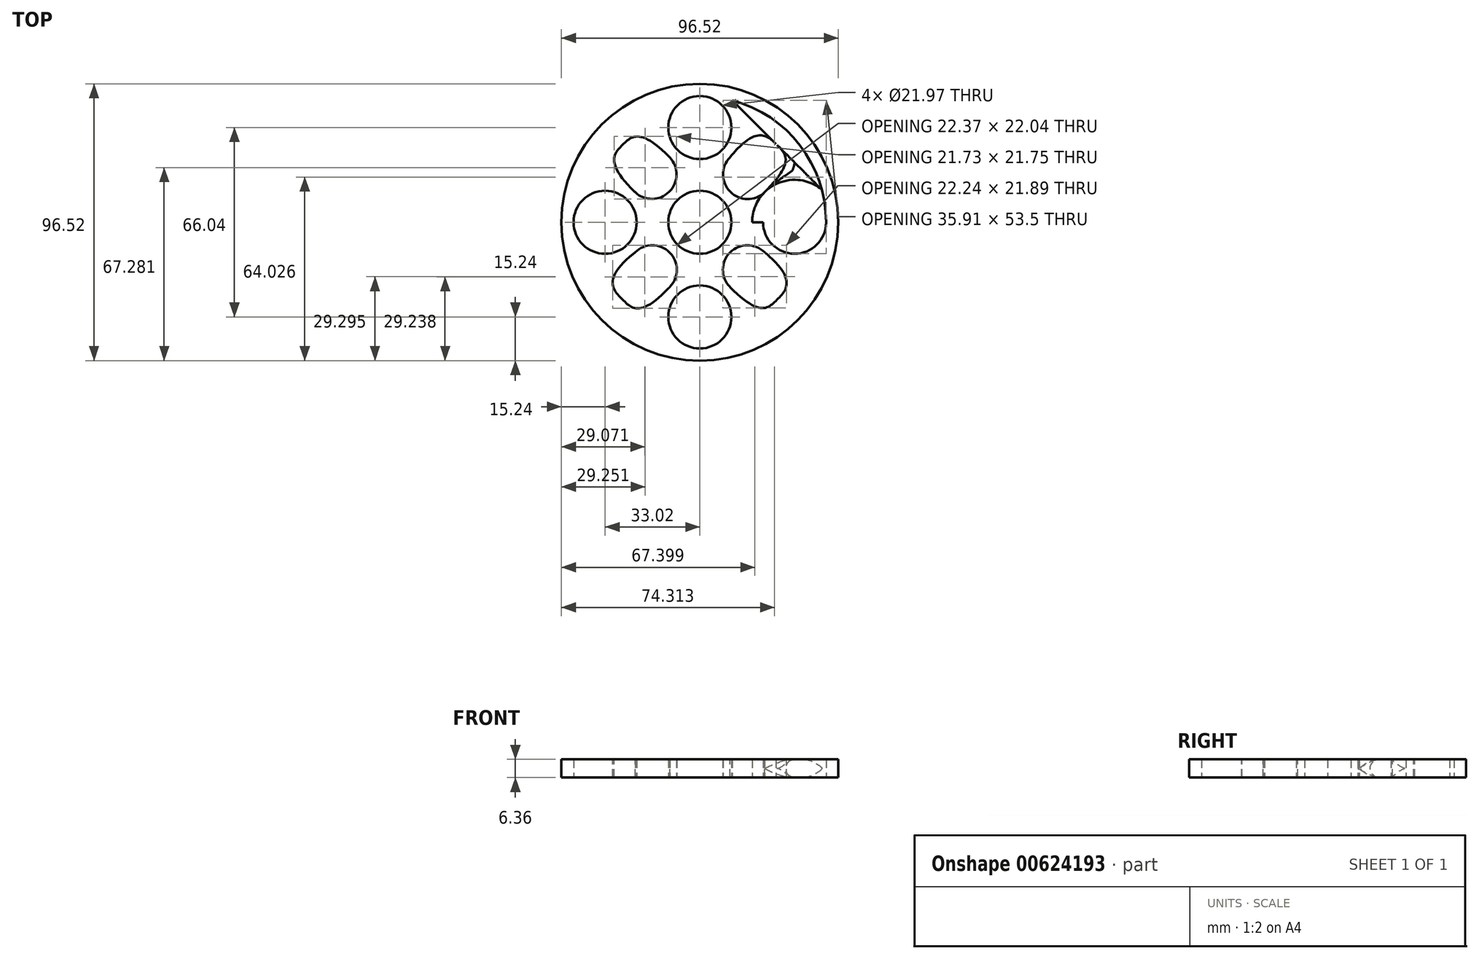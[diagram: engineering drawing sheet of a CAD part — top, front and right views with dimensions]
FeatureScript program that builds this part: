
annotation { "Feature Type Name" : "Feature", "Feature Type Description" : "" }
export const myFeature = defineFeature(function(context is Context, id is Id, definition is map)
    precondition{}
    {
        {
            var Q0;
            Q0=qCreatedBy(makeId("Top.planeOp"),FACE);
            var sketch = newSketch(context, id + "F0", { "sketchPlane" : qUnion([Q0])});
            skCircle(sketch, "E0", {"center": v(0, 0) * mm, "radius": 10.99 * mm});
            skCircle(sketch, "E1", {"center": v(0, 0) * mm, "radius": 14.8 * mm});
            skLineSegment(sketch, "E2", {"start": v(0, 0) * mm, "end": v(0, 33.02) * mm});
            skCircle(sketch, "E3", {"center": v(0, 33.02) * mm, "radius": 10.99 * mm});
            skCircle(sketch, "E4", {"center": v(0, 33.02) * mm, "radius": 14.8 * mm});
            skLineSegment(sketch, "E5.1.0", {"start": v(0, 0) * mm, "end": v(-33.02, 0) * mm});
            skCircle(sketch, "E5.1.1", {"center": v(-33.02, 0) * mm, "radius": 10.99 * mm});
            skCircle(sketch, "E5.1.2", {"center": v(-33.02, 0) * mm, "radius": 14.8 * mm});
            skLineSegment(sketch, "E5.2.0", {"start": v(0, 0) * mm, "end": v(0, -33.02) * mm});
            skCircle(sketch, "E5.2.1", {"center": v(0, -33.02) * mm, "radius": 10.99 * mm});
            skCircle(sketch, "E5.2.2", {"center": v(0, -33.02) * mm, "radius": 14.8 * mm});
            skLineSegment(sketch, "E6.2.3.0", {"start": v(0, 0) * mm, "end": v(33.02, 0) * mm});
            skCircle(sketch, "E6.3.3.0", {"center": v(33.02, 0) * mm, "radius": 10.99 * mm});
            skCircle(sketch, "E6.5.3.0", {"center": v(33.02, 0) * mm, "radius": 14.8 * mm});
            skPoint(sketch, "E7", {"position": v(-22.56, 10.46) * mm});
            skPoint(sketch, "E8", {"position": v(-10.46, 22.56) * mm});
            skPoint(sketch, "E9", {"position": v(10.46, 22.56) * mm});
            skPoint(sketch, "E10", {"position": v(22.56, 10.46) * mm});
            skPoint(sketch, "E11", {"position": v(22.56, -10.46) * mm});
            skPoint(sketch, "E12", {"position": v(10.46, -22.56) * mm});
            skPoint(sketch, "E13", {"position": v(-10.46, -22.56) * mm});
            skPoint(sketch, "E14", {"position": v(-22.56, -10.46) * mm});
            skArc(sketch, "E15", {"start": v(-22.56, 10.46) * mm, "mid": v(-10.65, 10.65) * mm, "end": v(-10.46, 22.56) * mm});
            skArc(sketch, "E16", {"start": v(10.46, 22.56) * mm, "mid": v(10.6, 10.6) * mm, "end": v(22.56, 10.46) * mm});
            skArc(sketch, "E17", {"start": v(22.56, -10.46) * mm, "mid": v(10.53, -10.53) * mm, "end": v(10.46, -22.56) * mm});
            skArc(sketch, "E18", {"start": v(-10.46, -22.56) * mm, "mid": v(-10.5, -10.5) * mm, "end": v(-22.56, -10.46) * mm});
            skCircle(sketch, "E19", {"center": v(0, 0) * mm, "radius": 44 * mm});
            skCircle(sketch, "E20", {"center": v(0, 0) * mm, "radius": 48.26 * mm});
            skLineSegment(sketch, "E21", {"start": v(42.52, 11.34) * mm, "end": v(11.34, 42.52) * mm});
            skLineSegment(sketch, "E22", {"start": v(-11.34, 42.52) * mm, "end": v(-42.49, 11.45) * mm});
            skLineSegment(sketch, "E23", {"start": v(-42.52, -11.34) * mm, "end": v(-11.45, -42.49) * mm});
            skLineSegment(sketch, "E24", {"start": v(11.34, -42.52) * mm, "end": v(42.49, -11.45) * mm});
            skFitSpline(sketch, "E25", {"points": [v(22.56, 10.46) * mm, v(26.93, 26.93) * mm, v(10.46, 22.56) * mm], "startDerivative": vector(62.37, 62.42) * mm, "endDerivative": vector(-55.65, -69.41) * mm});
            skFitSpline(sketch, "E26", {"points": [v(-10.46, 22.56) * mm, v(-26.92, 26.98) * mm, v(-22.56, 10.46) * mm], "startDerivative": vector(-61.8, 63.48) * mm, "endDerivative": vector(63.5, -61.8) * mm});
            skFitSpline(sketch, "E27", {"points": [v(-22.56, -10.46) * mm, v(-26.98, -26.92) * mm, v(-10.46, -22.56) * mm], "startDerivative": vector(-69.52, -55.75) * mm, "endDerivative": vector(60.94, 64.35) * mm});
            skFitSpline(sketch, "E28", {"points": [v(10.46, -22.56) * mm, v(26.92, -26.99) * mm, v(22.56, -10.46) * mm], "startDerivative": vector(62.67, -62.62) * mm, "endDerivative": vector(-68.67, 56.64) * mm});
            skSolve(sketch);
        }
        {
            var Q0;
            Q0=makeQuery(id+"F0.imprint","IMPRINT",FACE,{"disambiguationData":[TD([[makeQuery(id+"F0.imprint","IMPRINT",EDGE,{"derivedFrom":sQuery(id+"F0.wireOp",EDGE,"E5.1.1")}),-1.0]])]});
            var Q1;
            Q1=makeQuery(id+"F0.imprint","IMPRINT",FACE,{"disambiguationData":[TD([[makeQuery(id+"F0.imprint","IMPRINT",EDGE,{"derivedFrom":sQuery(id+"F0.wireOp",EDGE,"E5.2.1")}),-1.0]])]});
            var Q2;
            Q2=makeQuery(id+"F0.imprint","IMPRINT",FACE,{"disambiguationData":[TD([[makeQuery(id+"F0.imprint","IMPRINT",EDGE,{"derivedFrom":sQuery(id+"F0.wireOp",EDGE,"E6.3.3.0")}),-1.0]])]});
            var Q3;
            Q3=makeQuery(id+"F0.imprint","IMPRINT",FACE,{"disambiguationData":[TD([[makeQuery(id+"F0.imprint","IMPRINT",EDGE,{"derivedFrom":sQuery(id+"F0.wireOp",EDGE,"E3")}),-1.0]])]});
            var Q4;
            {var subQ0=sQuery(id+"F0.wireOp",EDGE,"E2");var subQ1=sQuery(id+"F0.wireOp",EDGE,"E0");var subQ2=makeQuery(id+"F0.imprint","INTERSECT",VERTEX,{"derivedFrom":[subQ1,subQ0]});Q4=makeQuery(id+"F0.imprint","IMPRINT",FACE,{"disambiguationData":[TD([[makeQuery(id+"F0.imprint","IMPRINT",EDGE,{"disambiguationData":[TD([[subQ2,1.0]])],"derivedFrom":subQ1}),-1.0]])]});}
            var Q5;
            {var subQ0=sQuery(id+"F0.wireOp",EDGE,"E6.2.3.0");var subQ1=sQuery(id+"F0.wireOp",EDGE,"E0");var subQ2=makeQuery(id+"F0.imprint","INTERSECT",VERTEX,{"derivedFrom":[subQ1,subQ0]});Q5=makeQuery(id+"F0.imprint","IMPRINT",FACE,{"disambiguationData":[TD([[makeQuery(id+"F0.imprint","IMPRINT",EDGE,{"disambiguationData":[TD([[subQ2,1.0]])],"derivedFrom":subQ1}),-1.0]])]});}
            var Q6;
            {var subQ0=sQuery(id+"F0.wireOp",EDGE,"E5.1.0");var subQ1=sQuery(id+"F0.wireOp",EDGE,"E0");var subQ2=makeQuery(id+"F0.imprint","INTERSECT",VERTEX,{"derivedFrom":[subQ1,subQ0]});Q6=makeQuery(id+"F0.imprint","IMPRINT",FACE,{"disambiguationData":[TD([[makeQuery(id+"F0.imprint","IMPRINT",EDGE,{"disambiguationData":[TD([[subQ2,-1.0]])],"derivedFrom":subQ1}),-1.0]])]});}
            var Q7;
            {var subQ0=sQuery(id+"F0.wireOp",EDGE,"E2");var subQ1=sQuery(id+"F0.wireOp",EDGE,"E0");var subQ2=makeQuery(id+"F0.imprint","INTERSECT",VERTEX,{"derivedFrom":[subQ1,subQ0]});Q7=makeQuery(id+"F0.imprint","IMPRINT",FACE,{"disambiguationData":[TD([[makeQuery(id+"F0.imprint","IMPRINT",EDGE,{"disambiguationData":[TD([[subQ2,-1.0]])],"derivedFrom":subQ1}),-1.0]])]});}
            var Q8;
            {var subQ5=sQuery(id+"F0.wireOp",EDGE,"E18");Q8=makeQuery(id+"F0.imprint","IMPRINT",FACE,{"disambiguationData":[TD([[makeQuery(id+"F0.imprint","IMPRINT",EDGE,{"derivedFrom":subQ5}),-1.0]])]});}
            var Q9;
            {var subQ5=sQuery(id+"F0.wireOp",EDGE,"E16");Q9=makeQuery(id+"F0.imprint","IMPRINT",FACE,{"disambiguationData":[TD([[makeQuery(id+"F0.imprint","IMPRINT",EDGE,{"derivedFrom":subQ5}),-1.0]])]});}
            var Q10;
            {var subQ5=sQuery(id+"F0.wireOp",EDGE,"E17");Q10=makeQuery(id+"F0.imprint","IMPRINT",FACE,{"disambiguationData":[TD([[makeQuery(id+"F0.imprint","IMPRINT",EDGE,{"derivedFrom":subQ5}),-1.0]])]});}
            var Q11;
            {var subQ5=sQuery(id+"F0.wireOp",EDGE,"E15");Q11=makeQuery(id+"F0.imprint","IMPRINT",FACE,{"disambiguationData":[TD([[makeQuery(id+"F0.imprint","IMPRINT",EDGE,{"derivedFrom":subQ5}),-1.0]])]});}
            var Q12;
            Q12=makeQuery(id+"F0.imprint","IMPRINT",FACE,{"disambiguationData":[TD([[makeQuery(id+"F0.imprint","IMPRINT",EDGE,{"derivedFrom":sQuery(id+"F0.wireOp",EDGE,"E20")}),1.0]])]});
            var Q13;
            {var subQ0=sQuery(id+"F0.wireOp",EDGE,"E19");var subQ1=sQuery(id+"F0.wireOp",EDGE,"E4");var subQ2=makeQuery(id+"F0.imprint","INTERSECT",VERTEX,{"disambiguationData":[OD(0.0)],"derivedFrom":[subQ1,subQ0]});Q13=makeQuery(id+"F0.imprint","IMPRINT",FACE,{"disambiguationData":[TD([[makeQuery(id+"F0.imprint","IMPRINT",EDGE,{"disambiguationData":[TD([[subQ2,1.0]])],"derivedFrom":subQ1}),1.0]])]});}
            var Q14;
            {var subQ0=sQuery(id+"F0.wireOp",EDGE,"E19");var subQ1=sQuery(id+"F0.wireOp",EDGE,"E5.1.2");var subQ2=makeQuery(id+"F0.imprint","INTERSECT",VERTEX,{"disambiguationData":[OD(0.0)],"derivedFrom":[subQ1,subQ0]});Q14=makeQuery(id+"F0.imprint","IMPRINT",FACE,{"disambiguationData":[TD([[makeQuery(id+"F0.imprint","IMPRINT",EDGE,{"disambiguationData":[TD([[subQ2,1.0]])],"derivedFrom":subQ1}),1.0]])]});}
            var Q15;
            {var subQ0=sQuery(id+"F0.wireOp",EDGE,"E19");var subQ1=sQuery(id+"F0.wireOp",EDGE,"E5.2.2");var subQ2=makeQuery(id+"F0.imprint","INTERSECT",VERTEX,{"disambiguationData":[OD(0.0)],"derivedFrom":[subQ1,subQ0]});Q15=makeQuery(id+"F0.imprint","IMPRINT",FACE,{"disambiguationData":[TD([[makeQuery(id+"F0.imprint","IMPRINT",EDGE,{"disambiguationData":[TD([[subQ2,1.0]])],"derivedFrom":subQ1}),1.0]])]});}
            var Q16;
            {var subQ0=sQuery(id+"F0.wireOp",EDGE,"E19");var subQ1=sQuery(id+"F0.wireOp",EDGE,"E6.5.3.0");var subQ2=makeQuery(id+"F0.imprint","INTERSECT",VERTEX,{"disambiguationData":[OD(0.0)],"derivedFrom":[subQ1,subQ0]});Q16=makeQuery(id+"F0.imprint","IMPRINT",FACE,{"disambiguationData":[TD([[makeQuery(id+"F0.imprint","IMPRINT",EDGE,{"disambiguationData":[TD([[subQ2,1.0]])],"derivedFrom":subQ1}),1.0]])]});}
            var Q17;
            {var subQ0=sQuery(id+"F0.wireOp",EDGE,"E25");var subQ3=sQuery(id+"F0.wireOp",EDGE,"E21");var subQ5=makeQuery(id+"F0.imprint","INTERSECT",VERTEX,{"derivedFrom":[subQ3,subQ0]});Q17=makeQuery(id+"F0.imprint","IMPRINT",FACE,{"disambiguationData":[TD([[makeQuery(id+"F0.imprint","IMPRINT",EDGE,{"disambiguationData":[TD([[subQ5,1.0]])],"derivedFrom":subQ3}),1.0]])]});}
            var Q18;
            {var subQ0=sQuery(id+"F0.wireOp",EDGE,"E25");var subQ3=sQuery(id+"F0.wireOp",EDGE,"E21");var subQ5=makeQuery(id+"F0.imprint","INTERSECT",VERTEX,{"derivedFrom":[subQ3,subQ0]});Q18=makeQuery(id+"F0.imprint","IMPRINT",FACE,{"disambiguationData":[TD([[makeQuery(id+"F0.imprint","IMPRINT",EDGE,{"disambiguationData":[TD([[subQ5,-1.0]])],"derivedFrom":subQ3}),1.0]])]});}
            var Q19;
            {var subQ0=sQuery(id+"F0.wireOp",EDGE,"E26");var subQ3=sQuery(id+"F0.wireOp",EDGE,"E22");var subQ5=makeQuery(id+"F0.imprint","INTERSECT",VERTEX,{"derivedFrom":[subQ3,subQ0]});Q19=makeQuery(id+"F0.imprint","IMPRINT",FACE,{"disambiguationData":[TD([[makeQuery(id+"F0.imprint","IMPRINT",EDGE,{"disambiguationData":[TD([[subQ5,1.0]])],"derivedFrom":subQ3}),1.0]])]});}
            var Q20;
            {var subQ3=sQuery(id+"F0.wireOp",EDGE,"E19");var subQ5=sQuery(id+"F0.wireOp",EDGE,"E22");var subQ6=makeQuery(id+"F0.imprint","INTERSECT",VERTEX,{"derivedFrom":[subQ3,subQ5]});Q20=makeQuery(id+"F0.imprint","IMPRINT",FACE,{"disambiguationData":[TD([[makeQuery(id+"F0.imprint","IMPRINT",EDGE,{"disambiguationData":[TD([[subQ6,-1.0]])],"derivedFrom":subQ3}),1.0]])]});}
            var Q21;
            {var subQ0=sQuery(id+"F0.wireOp",EDGE,"E27");var subQ3=sQuery(id+"F0.wireOp",EDGE,"E23");var subQ5=makeQuery(id+"F0.imprint","INTERSECT",VERTEX,{"derivedFrom":[subQ3,subQ0]});Q21=makeQuery(id+"F0.imprint","IMPRINT",FACE,{"disambiguationData":[TD([[makeQuery(id+"F0.imprint","IMPRINT",EDGE,{"disambiguationData":[TD([[subQ5,1.0]])],"derivedFrom":subQ3}),1.0]])]});}
            var Q22;
            {var subQ3=sQuery(id+"F0.wireOp",EDGE,"E19");var subQ5=sQuery(id+"F0.wireOp",EDGE,"E23");var subQ6=makeQuery(id+"F0.imprint","INTERSECT",VERTEX,{"derivedFrom":[subQ3,subQ5]});Q22=makeQuery(id+"F0.imprint","IMPRINT",FACE,{"disambiguationData":[TD([[makeQuery(id+"F0.imprint","IMPRINT",EDGE,{"disambiguationData":[TD([[subQ6,-1.0]])],"derivedFrom":subQ3}),1.0]])]});}
            var Q23;
            {var subQ0=sQuery(id+"F0.wireOp",EDGE,"E28");var subQ3=sQuery(id+"F0.wireOp",EDGE,"E24");var subQ5=makeQuery(id+"F0.imprint","INTERSECT",VERTEX,{"derivedFrom":[subQ3,subQ0]});Q23=makeQuery(id+"F0.imprint","IMPRINT",FACE,{"disambiguationData":[TD([[makeQuery(id+"F0.imprint","IMPRINT",EDGE,{"disambiguationData":[TD([[subQ5,1.0]])],"derivedFrom":subQ3}),1.0]])]});}
            var Q24;
            {var subQ3=sQuery(id+"F0.wireOp",EDGE,"E19");var subQ5=sQuery(id+"F0.wireOp",EDGE,"E24");var subQ6=makeQuery(id+"F0.imprint","INTERSECT",VERTEX,{"derivedFrom":[subQ3,subQ5]});Q24=makeQuery(id+"F0.imprint","IMPRINT",FACE,{"disambiguationData":[TD([[makeQuery(id+"F0.imprint","IMPRINT",EDGE,{"disambiguationData":[TD([[subQ6,-1.0]])],"derivedFrom":subQ3}),1.0]])]});}
            var Q25;
            {var subQ0=sQuery(id+"F0.wireOp",EDGE,"E19");var subQ4=makeQuery(id+"F0.imprint","INTERSECT",VERTEX,{"derivedFrom":[sQuery(id+"F0.wireOp",EDGE,"E6.3.3.0"),subQ0]});Q25=makeQuery(id+"F0.imprint","IMPRINT",FACE,{"disambiguationData":[TD([[makeQuery(id+"F0.imprint","IMPRINT",EDGE,{"disambiguationData":[TD([[subQ4,1.0]])],"derivedFrom":subQ0}),-1.0]])]});}
            var Q26;
            {var subQ0=sQuery(id+"F0.wireOp",EDGE,"E19");var subQ4=makeQuery(id+"F0.imprint","INTERSECT",VERTEX,{"derivedFrom":[sQuery(id+"F0.wireOp",EDGE,"E5.2.1"),subQ0]});Q26=makeQuery(id+"F0.imprint","IMPRINT",FACE,{"disambiguationData":[TD([[makeQuery(id+"F0.imprint","IMPRINT",EDGE,{"disambiguationData":[TD([[subQ4,1.0]])],"derivedFrom":subQ0}),-1.0]])]});}
            var Q27;
            {var subQ0=sQuery(id+"F0.wireOp",EDGE,"E19");var subQ4=makeQuery(id+"F0.imprint","INTERSECT",VERTEX,{"derivedFrom":[sQuery(id+"F0.wireOp",EDGE,"E5.1.1"),subQ0]});Q27=makeQuery(id+"F0.imprint","IMPRINT",FACE,{"disambiguationData":[TD([[makeQuery(id+"F0.imprint","IMPRINT",EDGE,{"disambiguationData":[TD([[subQ4,1.0]])],"derivedFrom":subQ0}),-1.0]])]});}
            var Q28;
            {var subQ0=sQuery(id+"F0.wireOp",EDGE,"E19");var subQ1=sQuery(id+"F0.wireOp",EDGE,"E5.1.2");var subQ3=makeQuery(id+"F0.imprint","INTERSECT",VERTEX,{"derivedFrom":[subQ1,subQ0]});Q28=makeQuery(id+"F0.imprint","IMPRINT",FACE,{"disambiguationData":[TD([[makeQuery(id+"F0.imprint","IMPRINT",EDGE,{"disambiguationData":[TD([[subQ3,-1.0]])],"derivedFrom":subQ1}),1.0]])]});}
            var Q29;
            {var subQ1=sQuery(id+"F0.wireOp",EDGE,"E6.5.3.0");var subQ8=makeQuery(id+"F0.imprint","IMPRINT",VERTEX,{"derivedFrom":subQ1});Q29=makeQuery(id+"F0.imprint","IMPRINT",FACE,{"disambiguationData":[TD([[makeQuery(id+"F0.imprint","IMPRINT",EDGE,{"disambiguationData":[TD([[subQ8,1.0]])],"derivedFrom":subQ1}),1.0]])]});}
            var Q30;
            {var subQ0=sQuery(id+"F0.wireOp",EDGE,"E19");var subQ1=sQuery(id+"F0.wireOp",EDGE,"E5.2.2");var subQ3=makeQuery(id+"F0.imprint","INTERSECT",VERTEX,{"derivedFrom":[subQ1,subQ0]});Q30=makeQuery(id+"F0.imprint","IMPRINT",FACE,{"disambiguationData":[TD([[makeQuery(id+"F0.imprint","IMPRINT",EDGE,{"disambiguationData":[TD([[subQ3,-1.0]])],"derivedFrom":subQ1}),1.0]])]});}
            var Q31;
            {var subQ0=sQuery(id+"F0.wireOp",EDGE,"E23");var subQ1=sQuery(id+"F0.wireOp",EDGE,"E19");var subQ3=makeQuery(id+"F0.imprint","INTERSECT",VERTEX,{"derivedFrom":[subQ1,subQ0]});Q31=makeQuery(id+"F0.imprint","IMPRINT",FACE,{"disambiguationData":[TD([[makeQuery(id+"F0.imprint","IMPRINT",EDGE,{"disambiguationData":[TD([[subQ3,1.0]])],"derivedFrom":subQ0}),-1.0]])]});}
            var Q32;
            {var subQ0=sQuery(id+"F0.wireOp",EDGE,"E24");var subQ1=sQuery(id+"F0.wireOp",EDGE,"E19");var subQ3=makeQuery(id+"F0.imprint","INTERSECT",VERTEX,{"derivedFrom":[subQ1,subQ0]});Q32=makeQuery(id+"F0.imprint","IMPRINT",FACE,{"disambiguationData":[TD([[makeQuery(id+"F0.imprint","IMPRINT",EDGE,{"disambiguationData":[TD([[subQ3,1.0]])],"derivedFrom":subQ0}),-1.0]])]});}
            var Q33;
            {var subQ0=sQuery(id+"F0.wireOp",EDGE,"E21");var subQ4=sQuery(id+"F0.wireOp",EDGE,"E25");var subQ6=makeQuery(id+"F0.imprint","INTERSECT",VERTEX,{"disambiguationData":[OD(0.0)],"derivedFrom":[subQ0,subQ4]});Q33=makeQuery(id+"F0.imprint","IMPRINT",FACE,{"disambiguationData":[TD([[makeQuery(id+"F0.imprint","IMPRINT",EDGE,{"disambiguationData":[TD([[subQ6,-1.0]])],"derivedFrom":subQ4}),-1.0]])]});}
            var Q34;
            {var subQ0=sQuery(id+"F0.wireOp",EDGE,"E22");var subQ1=sQuery(id+"F0.wireOp",EDGE,"E19");var subQ3=makeQuery(id+"F0.imprint","INTERSECT",VERTEX,{"derivedFrom":[subQ1,subQ0]});Q34=makeQuery(id+"F0.imprint","IMPRINT",FACE,{"disambiguationData":[TD([[makeQuery(id+"F0.imprint","IMPRINT",EDGE,{"disambiguationData":[TD([[subQ3,1.0]])],"derivedFrom":subQ0}),-1.0]])]});}
            extrude(context, id + "F1", {"entities" : qUnion([Q0, Q1, Q2, Q3, Q4, Q5, Q6, Q7, Q8, Q9, Q10, Q11, Q12, Q13, Q14, Q15, Q16, Q17, Q18, Q19, Q20, Q21, Q22, Q23, Q24, Q25, Q26, Q27, Q28, Q29, Q30, Q31, Q32, Q33, Q34]), "endBound" : BoundingType.SYMMETRIC, "depth" : 6.35 * mm, "offsetDistance" : 25.4 * mm});
        }
        {
            var Q0;
            Q0=makeQuery(id+"F1.opExtrude","CAP_EDGE",EDGE,{"disambiguationData":[OSD([sQuery(id+"F0.wireOp",EDGE,"E15")])],"isStart":false});
            var Q1;
            Q1=makeQuery(id+"F1.opExtrude","CAP_EDGE",EDGE,{"disambiguationData":[OSD([sQuery(id+"F0.wireOp",EDGE,"E26")])],"isStart":false});
            var Q2;
            Q2=makeQuery(id+"F1.opExtrude","CAP_EDGE",EDGE,{"disambiguationData":[OSD([sQuery(id+"F0.wireOp",EDGE,"E16")])],"isStart":false});
            var Q3;
            Q3=makeQuery(id+"F1.opExtrude","CAP_EDGE",EDGE,{"disambiguationData":[OSD([sQuery(id+"F0.wireOp",EDGE,"E25")])],"isStart":false});
            var Q4;
            Q4=makeQuery(id+"F1.opExtrude","CAP_EDGE",EDGE,{"disambiguationData":[OSD([sQuery(id+"F0.wireOp",EDGE,"E6.5.3.0")])],"isStart":false});
            var Q5;
            Q5=makeQuery(id+"F1.opExtrude","CAP_EDGE",EDGE,{"disambiguationData":[OSD([sQuery(id+"F0.wireOp",EDGE,"E17")])],"isStart":false});
            var Q6;
            Q6=makeQuery(id+"F1.opExtrude","CAP_EDGE",EDGE,{"disambiguationData":[OSD([sQuery(id+"F0.wireOp",EDGE,"E28")])],"isStart":false});
            var Q7;
            Q7=makeQuery(id+"F1.opExtrude","CAP_EDGE",EDGE,{"disambiguationData":[OSD([sQuery(id+"F0.wireOp",EDGE,"E27")])],"isStart":false});
            var Q8;
            Q8=makeQuery(id+"F1.opExtrude","CAP_EDGE",EDGE,{"disambiguationData":[OSD([sQuery(id+"F0.wireOp",EDGE,"E18")])],"isStart":false});
            var Q9;
            Q9=makeQuery(id+"F1.opExtrude","CAP_EDGE",EDGE,{"disambiguationData":[OSD([sQuery(id+"F0.wireOp",EDGE,"E20")])],"isStart":false});
            var Q10;
            Q10=makeQuery(id+"F1.opExtrude","CAP_EDGE",EDGE,{"disambiguationData":[OSD([sQuery(id+"F0.wireOp",EDGE,"E20")])],"isStart":true});
            var Q11;
            Q11=makeQuery(id+"F1.opExtrude","CAP_EDGE",EDGE,{"disambiguationData":[OSD([sQuery(id+"F0.wireOp",EDGE,"E15")])],"isStart":true});
            var Q12;
            Q12=makeQuery(id+"F1.opExtrude","CAP_EDGE",EDGE,{"disambiguationData":[OSD([sQuery(id+"F0.wireOp",EDGE,"E26")])],"isStart":true});
            var Q13;
            Q13=makeQuery(id+"F1.opExtrude","CAP_EDGE",EDGE,{"disambiguationData":[OSD([sQuery(id+"F0.wireOp",EDGE,"E25")])],"isStart":true});
            var Q14;
            Q14=makeQuery(id+"F1.opExtrude","CAP_EDGE",EDGE,{"disambiguationData":[OSD([sQuery(id+"F0.wireOp",EDGE,"E6.5.3.0")])],"isStart":true});
            var Q15;
            Q15=makeQuery(id+"F1.opExtrude","CAP_EDGE",EDGE,{"disambiguationData":[OSD([sQuery(id+"F0.wireOp",EDGE,"E28")])],"isStart":true});
            var Q16;
            Q16=makeQuery(id+"F1.opExtrude","CAP_EDGE",EDGE,{"disambiguationData":[OSD([sQuery(id+"F0.wireOp",EDGE,"E17")])],"isStart":true});
            var Q17;
            Q17=makeQuery(id+"F1.opExtrude","CAP_EDGE",EDGE,{"disambiguationData":[OSD([sQuery(id+"F0.wireOp",EDGE,"E27")])],"isStart":true});
            var Q18;
            Q18=makeQuery(id+"F1.opExtrude","CAP_EDGE",EDGE,{"disambiguationData":[OSD([sQuery(id+"F0.wireOp",EDGE,"E18")])],"isStart":true});
            fillet(context, id + "F2", {"entities" : qUnion([Q0, Q1, Q2, Q3, Q4, Q5, Q6, Q7, Q8, Q9, Q10, Q11, Q12, Q13, Q14, Q15, Q16, Q17, Q18]), "radius" : 3.17 * mm, "tangentPropagation" : true, "allowEdgeOverflow" : false});
        }
    });
